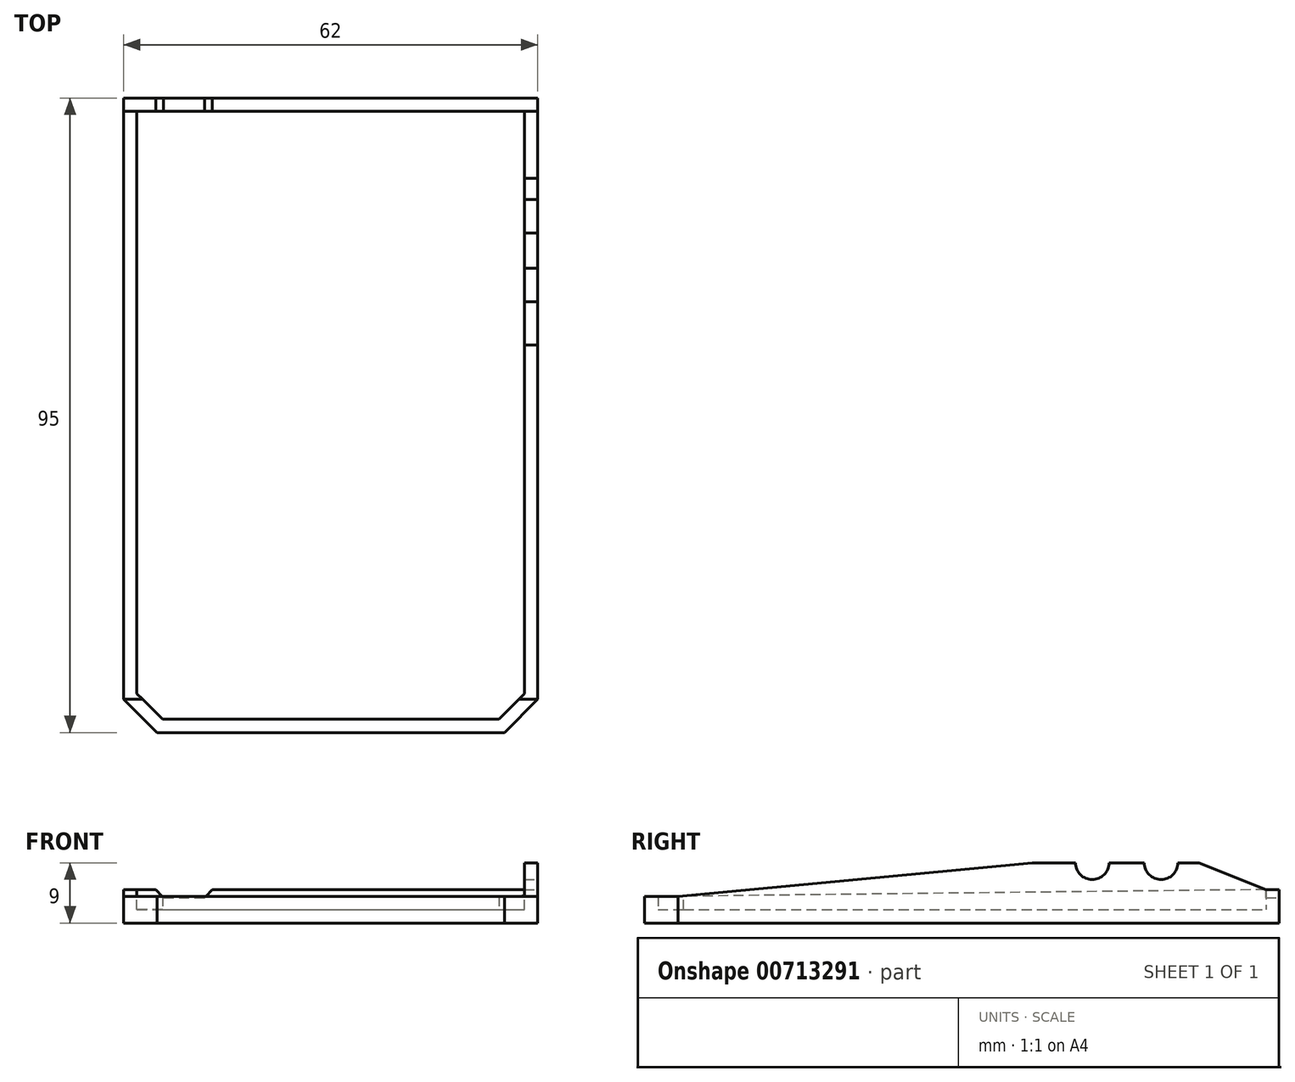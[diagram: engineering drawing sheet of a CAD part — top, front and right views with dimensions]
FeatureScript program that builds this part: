
annotation { "Feature Type Name" : "Feature", "Feature Type Description" : "" }
export const myFeature = defineFeature(function(context is Context, id is Id, definition is map)
    precondition{}
    {
        {
            var Q0;
            Q0=qCreatedBy(makeId("Top.planeOp"),FACE);
            var sketch = newSketch(context, id + "F0", { "sketchPlane" : qUnion([Q0])});
            skLineSegment(sketch, "E0.bottom", {"start": v(-31, -47.5) * mm, "end": v(31, -47.5) * mm});
            skLineSegment(sketch, "E0.top", {"start": v(-31, 47.5) * mm, "end": v(31, 47.5) * mm});
            skLineSegment(sketch, "E0.left", {"start": v(-31, -47.5) * mm, "end": v(-31, 47.5) * mm});
            skLineSegment(sketch, "E0.right", {"start": v(31, -47.5) * mm, "end": v(31, 47.5) * mm});
            skPoint(sketch, "E0.middle", {"position": v(0, 0) * mm});
            skSolve(sketch);
        }
        {
            var Q0;
            Q0=makeQuery(id+"F0.imprint","IMPRINT",FACE,{"disambiguationData":[TD([[makeQuery(id+"F0.imprint","IMPRINT",EDGE,{"derivedFrom":sQuery(id+"F0.wireOp",EDGE,"E0.bottom")}),1.0]])]});
            extrude(context, id + "F1", {"entities" : qUnion([Q0]), "depth" : 9 * mm, "offsetDistance" : 25 * mm});
        }
        {
            var Q0;
            Q0=makeQuery(id+"F1.opExtrude","SWEPT_EDGE",EDGE,{"disambiguationData":[OSD([sQuery(id+"F0.wireOp",EDGE,"E0.bottom"),sQuery(id+"F0.wireOp",EDGE,"E0.left")])]});
            var Q1;
            Q1=makeQuery(id+"F1.opExtrude","SWEPT_EDGE",EDGE,{"disambiguationData":[OSD([sQuery(id+"F0.wireOp",EDGE,"E0.bottom"),sQuery(id+"F0.wireOp",EDGE,"E0.right")])]});
            chamfer(context, id + "F2", {"entities" : qUnion([Q0, Q1]), "width" : 5 * mm, "tangentPropagation" : true});
        }
        {
            var Q0;
            Q0=makeQuery(id+"F1.opExtrude","CAP_FACE",FACE,{"disambiguationData":[OSD([sQuery(id+"F0.wireOp",EDGE,"E0.bottom"),sQuery(id+"F0.wireOp",EDGE,"E0.top"),sQuery(id+"F0.wireOp",EDGE,"E0.left"),sQuery(id+"F0.wireOp",EDGE,"E0.right")])],"isStart":false});
            shell(context, id + "F3", {"entities" : qUnion([Q0]), "thickness" : 2 * mm});
        }
        {
            var Q0;
            Q0=makeQuery(id+"F1.opExtrude","SWEPT_FACE",FACE,{"disambiguationData":[OSD([sQuery(id+"F0.wireOp",EDGE,"E0.right")])]});
            var sketch = newSketch(context, id + "F4", { "sketchPlane" : qUnion([Q0])});
            skLineSegment(sketch, "E1", {"start": v(32.3, 9) * mm, "end": v(35.5, 9) * mm});
            skLineSegment(sketch, "E2", {"start": v(47.5, 5) * mm, "end": v(47.5, 10) * mm});
            skLineSegment(sketch, "E3", {"start": v(47.5, 10) * mm, "end": v(-47.5, 10) * mm});
            skLineSegment(sketch, "E4", {"start": v(10.5, 9) * mm, "end": v(-42.5, 4) * mm});
            skLineSegment(sketch, "E5", {"start": v(-42.5, 4) * mm, "end": v(-47.5, 4) * mm});
            skLineSegment(sketch, "E6", {"start": v(-47.5, 4) * mm, "end": v(-47.5, 10) * mm});
            skArc(sketch, "E7", {"start": v(32.3, 9) * mm, "mid": v(29.8, 6.5) * mm, "end": v(27.3, 9) * mm});
            skLineSegment(sketch, "E8", {"start": v(27.3, 9) * mm, "end": v(22, 9) * mm});
            skArc(sketch, "E9", {"start": v(22, 9) * mm, "mid": v(19.5, 6.5) * mm, "end": v(17, 9) * mm});
            skLineSegment(sketch, "E10", {"start": v(17, 9) * mm, "end": v(10.5, 9) * mm});
            skLineSegment(sketch, "E11", {"start": v(47.5, 5) * mm, "end": v(45.5, 5) * mm});
            skLineSegment(sketch, "E12", {"start": v(45.5, 5) * mm, "end": v(35.5, 9) * mm});
            skSolve(sketch);
        }
        {
            var Q0;
            Q0 = qSketchRegion(id + "F4", true);
            extrude(context, id + "F5", {"entities" : qUnion([Q0]), "operationType" : NewBodyOperationType.REMOVE, "oppositeDirection" : true, "depth" : 2 * mm, "offsetDistance" : 25 * mm});
        }
        {
            var Q0;
            Q0=makeQuery(id+"F1.opExtrude","SWEPT_FACE",FACE,{"disambiguationData":[OSD([sQuery(id+"F0.wireOp",EDGE,"E0.top")])]});
            var sketch = newSketch(context, id + "F6", { "sketchPlane" : qUnion([Q0])});
            skLineSegment(sketch, "E13", {"start": v(-29, 5) * mm, "end": v(-29, 9) * mm});
            skLineSegment(sketch, "E14", {"start": v(-29, 9) * mm, "end": v(31, 9) * mm});
            skLineSegment(sketch, "E15", {"start": v(31, 9) * mm, "end": v(31, 5) * mm});
            skLineSegment(sketch, "E16", {"start": v(31, 5) * mm, "end": v(26.2, 5) * mm});
            skLineSegment(sketch, "E17", {"start": v(26.2, 5) * mm, "end": v(25, 3.8) * mm});
            skLineSegment(sketch, "E18", {"start": v(25, 3.8) * mm, "end": v(18.9, 3.8) * mm});
            skLineSegment(sketch, "E19", {"start": v(18.9, 3.8) * mm, "end": v(17.7, 5) * mm});
            skLineSegment(sketch, "E20", {"start": v(17.7, 5) * mm, "end": v(-25.94, 5) * mm});
            skLineSegment(sketch, "E21", {"start": v(-25.94, 5) * mm, "end": v(-29, 5) * mm});
            skSolve(sketch);
        }
        {
            var Q0;
            Q0 = qSketchRegion(id + "F6", true);
            extrude(context, id + "F7", {"entities" : qUnion([Q0]), "operationType" : NewBodyOperationType.REMOVE, "oppositeDirection" : true, "depth" : 2 * mm, "offsetDistance" : 25 * mm});
        }
        {
            var Q0;
            {var subQ2=sQuery(id+"F4.wireOp",EDGE,"E5");var subQ3=sQuery(id+"F4.wireOp",EDGE,"E4");Q0=makeQuery(id+"F5.boolean.opBoolean","COPY",FACE,{"disambiguationData":[TD([makeQuery(id+"F5.opExtrude","SWEPT_FACE",FACE,{"disambiguationData":[OSD([subQ3])]})])],"derivedFrom":makeQuery(id+"F5.opExtrude","CAP_FACE",FACE,{"disambiguationData":[OSD([sQuery(id+"F4.wireOp",EDGE,"E1"),sQuery(id+"F4.wireOp",EDGE,"OcuAVjW9-qdYi-LsHF-kZv1-YlmOSk6GTqZC"),sQuery(id+"F4.wireOp",EDGE,"E2"),sQuery(id+"F4.wireOp",EDGE,"E3"),subQ3,subQ2,sQuery(id+"F4.wireOp",EDGE,"E6"),sQuery(id+"F4.wireOp",EDGE,"E7"),sQuery(id+"F4.wireOp",EDGE,"E8"),sQuery(id+"F4.wireOp",EDGE,"E9"),sQuery(id+"F4.wireOp",EDGE,"E10")])],"isStart":false})});}
            extrude(context, id + "F8", {"entities" : qUnion([Q0]), "operationType" : NewBodyOperationType.ADD, "depth" : 25 * mm, "offsetDistance" : 25 * mm});
        }
        {
            var Q0;
            Q0=makeQuery(id+"F8.opExtrude","CAP_FACE",FACE,{"disambiguationData":[OSD([sQuery(id+"F4.wireOp",EDGE,"E1"),sQuery(id+"F4.wireOp",EDGE,"OcuAVjW9-qdYi-LsHF-kZv1-YlmOSk6GTqZC"),sQuery(id+"F4.wireOp",EDGE,"E2"),sQuery(id+"F4.wireOp",EDGE,"E3"),sQuery(id+"F4.wireOp",EDGE,"E4"),sQuery(id+"F4.wireOp",EDGE,"E5"),sQuery(id+"F4.wireOp",EDGE,"E6"),sQuery(id+"F4.wireOp",EDGE,"E7"),sQuery(id+"F4.wireOp",EDGE,"E8"),sQuery(id+"F4.wireOp",EDGE,"E9"),sQuery(id+"F4.wireOp",EDGE,"E10")])],"isStart":false});
            var sketch = newSketch(context, id + "F9", { "sketchPlane" : qUnion([Q0])});
            skLineSegment(sketch, "E22", {"start": v(-41.67, 4.08) * mm, "end": v(-42.5, 4) * mm});
            skLineSegment(sketch, "E23", {"start": v(-42.5, 4) * mm, "end": v(-47.5, 4) * mm});
            skLineSegment(sketch, "E24", {"start": v(-47.5, 4) * mm, "end": v(-47.5, 9.37) * mm});
            skLineSegment(sketch, "E25", {"start": v(-41.67, 4.08) * mm, "end": v(-41.67, 9.37) * mm});
            skLineSegment(sketch, "E26", {"start": v(-41.67, 9.37) * mm, "end": v(-47.5, 9.37) * mm});
            skSolve(sketch);
        }
        {
            var Q0;
            Q0 = qSketchRegion(id + "F9", true);
            extrude(context, id + "F10", {"entities" : qUnion([Q0]), "operationType" : NewBodyOperationType.REMOVE, "oppositeDirection" : true, "depth" : 90 * mm, "offsetDistance" : 25 * mm});
        }
        {
            var Q0;
            Q0=makeQuery(id+"F1.opExtrude","SWEPT_FACE",FACE,{"disambiguationData":[OSD([sQuery(id+"F0.wireOp",EDGE,"E0.left")])]});
            var sketch = newSketch(context, id + "F11", { "sketchPlane" : qUnion([Q0])});
            skLineSegment(sketch, "E27", {"start": v(-45.5, 5) * mm, "end": v(42.5, 4) * mm});
            skLineSegment(sketch, "E28", {"start": v(42.5, 4) * mm, "end": v(42.56, 9) * mm});
            skLineSegment(sketch, "E29", {"start": v(42.56, 9) * mm, "end": v(-45.5, 9) * mm});
            skLineSegment(sketch, "E30", {"start": v(-45.5, 9) * mm, "end": v(-45.5, 5) * mm});
            skSolve(sketch);
        }
        {
            var Q0;
            Q0 = qSketchRegion(id + "F11", true);
            extrude(context, id + "F12", {"entities" : qUnion([Q0]), "operationType" : NewBodyOperationType.REMOVE, "oppositeDirection" : true, "depth" : 3 * mm, "offsetDistance" : 25 * mm});
        }
    });
